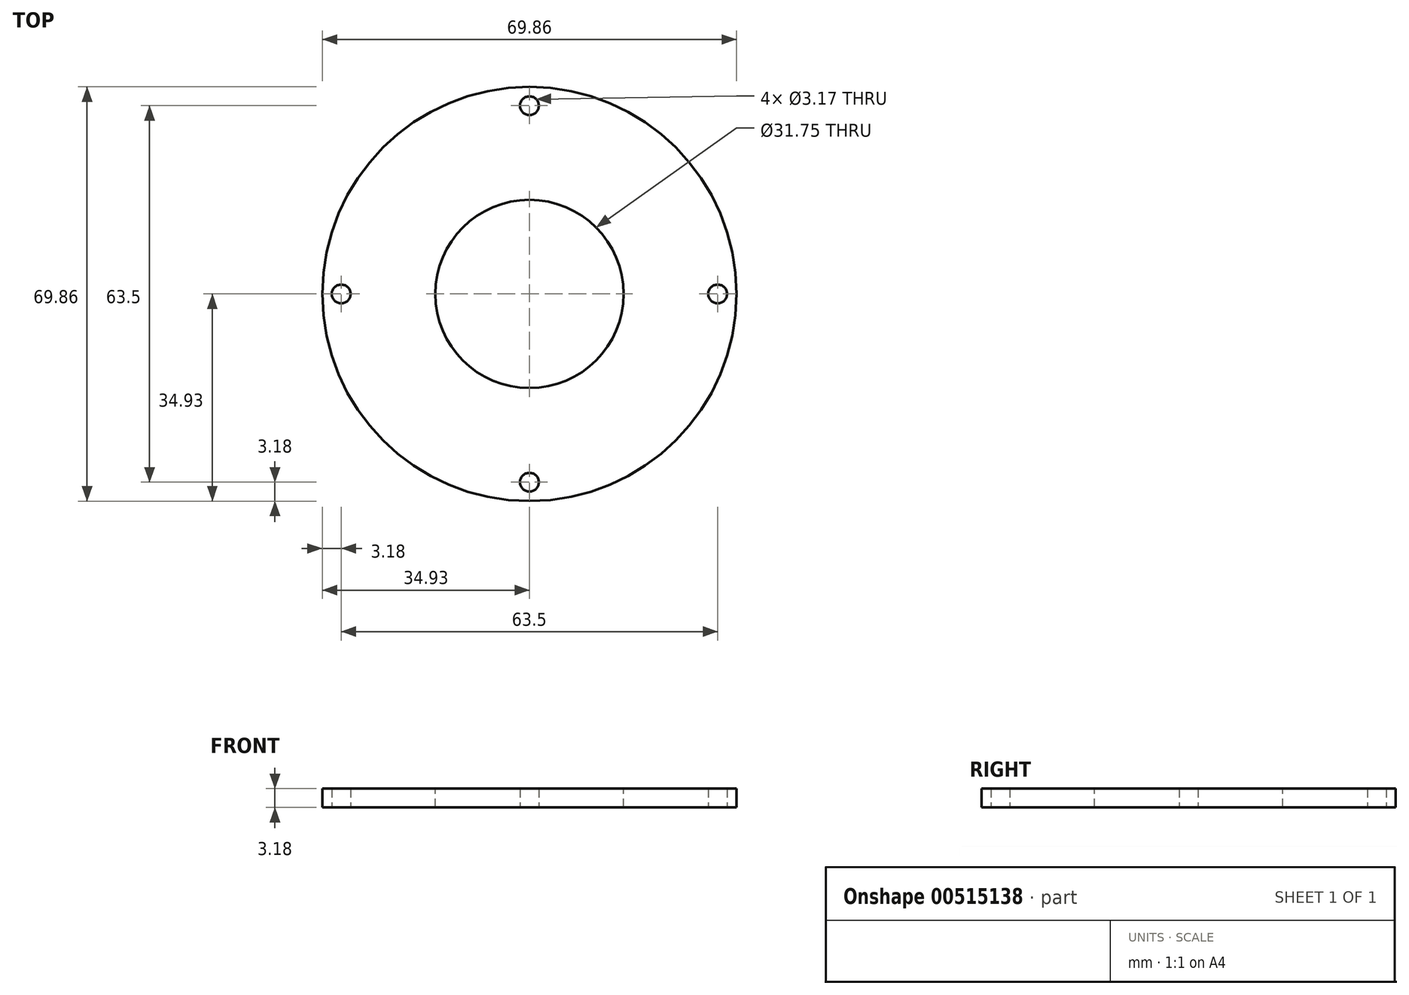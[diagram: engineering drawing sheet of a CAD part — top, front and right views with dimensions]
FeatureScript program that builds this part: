
annotation { "Feature Type Name" : "Feature", "Feature Type Description" : "" }
export const myFeature = defineFeature(function(context is Context, id is Id, definition is map)
    precondition{}
    {
        {
            var Q0;
            Q0=qCreatedBy(makeId("Top.planeOp"),FACE);
            var sketch = newSketch(context, id + "F0", { "sketchPlane" : qUnion([Q0])});
            skCircle(sketch, "E0", {"center": v(0, 0) * mm, "radius": 34.93 * mm});
            skLineSegment(sketch, "E1", {"start": v(0, -30.16) * mm, "end": v(0, -34.93) * mm});
            skLineSegment(sketch, "E2", {"start": v(0, -34.93) * mm, "end": v(0, -30.16) * mm});
            skLineSegment(sketch, "E3", {"start": v(0, 34.93) * mm, "end": v(0, 30.16) * mm});
            skLineSegment(sketch, "E4", {"start": v(30.16, 0) * mm, "end": v(34.93, 0) * mm});
            skLineSegment(sketch, "E5", {"start": v(34.93, 0) * mm, "end": v(30.16, 0) * mm});
            skCircle(sketch, "E6", {"center": v(0, 31.75) * mm, "radius": 1.59 * mm});
            skCircle(sketch, "E7", {"center": v(0, -31.75) * mm, "radius": 1.59 * mm});
            skCircle(sketch, "E8", {"center": v(31.75, 0) * mm, "radius": 1.59 * mm});
            skCircle(sketch, "E9", {"center": v(-31.75, 0) * mm, "radius": 1.59 * mm});
            skLineSegment(sketch, "E10.trimOffspring", {"start": v(-30.16, 0) * mm, "end": v(-34.93, 0) * mm});
            skLineSegment(sketch, "E11.trimOffspring", {"start": v(0, 30.16) * mm, "end": v(0, 34.93) * mm});
            skSolve(sketch);
        }
        {
            var Q0;
            Q0 = qSketchRegion(id + "F0", true);
            extrude(context, id + "F1", {"entities" : qUnion([Q0]), "depth" : 3.17 * mm, "offsetDistance" : 25.4 * mm});
        }
        {
            var Q0;
            Q0=makeQuery(id+"F1.opExtrude","CAP_FACE",FACE,{"disambiguationData":[OSD([sQuery(id+"F0.wireOp",EDGE,"E0"),sQuery(id+"F0.wireOp",EDGE,"E6"),sQuery(id+"F0.wireOp",EDGE,"E7"),sQuery(id+"F0.wireOp",EDGE,"E8"),sQuery(id+"F0.wireOp",EDGE,"E9")])],"isStart":false});
            var sketch = newSketch(context, id + "F2", { "sketchPlane" : qUnion([Q0])});
            skCircle(sketch, "E12", {"center": v(0, 0) * mm, "radius": 15.88 * mm});
            skSolve(sketch);
        }
        {
            var Q0;
            Q0 = qSketchRegion(id + "F2", true);
            extrude(context, id + "F3", {"entities" : qUnion([Q0]), "operationType" : NewBodyOperationType.REMOVE, "oppositeDirection" : true, "depth" : 25.4 * mm, "offsetDistance" : 25.4 * mm});
        }
    });
